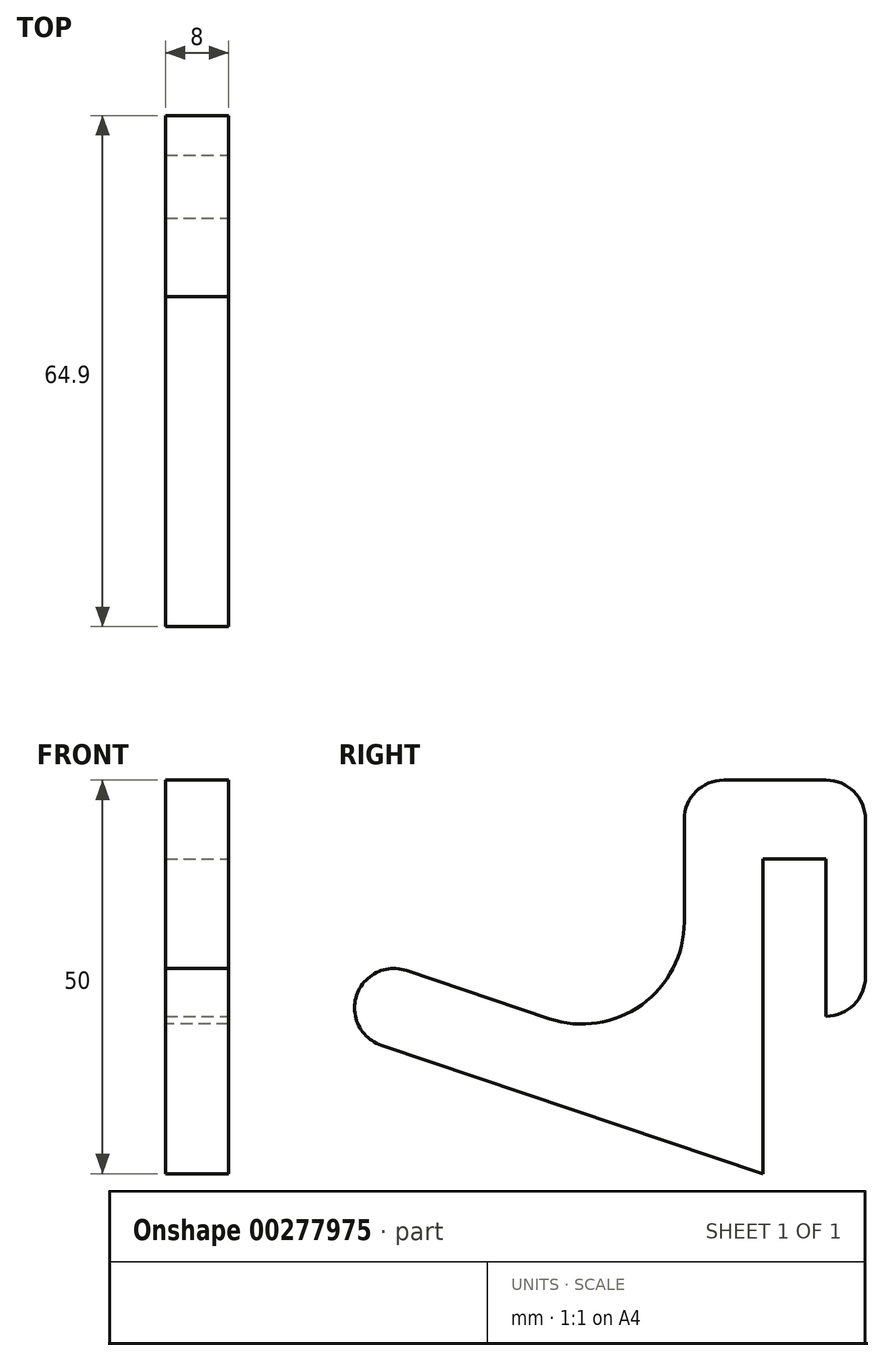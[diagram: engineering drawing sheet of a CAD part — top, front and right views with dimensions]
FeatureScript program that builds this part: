
annotation { "Feature Type Name" : "Feature", "Feature Type Description" : "" }
export const myFeature = defineFeature(function(context is Context, id is Id, definition is map)
    precondition{}
    {
        {
            var Q0;
            Q0=qCreatedBy(makeId("Right.planeOp"),FACE);
            var sketch = newSketch(context, id + "F0", { "sketchPlane" : qUnion([Q0])});
            skLineSegment(sketch, "E0", {"start": v(-11.66, 240.6) * mm, "end": v(-11.66, 204.52) * mm});
            skLineSegment(sketch, "E1", {"start": v(-1.66, 190.6) * mm, "end": v(-54.9, 208.51) * mm});
            skLineSegment(sketch, "E2.0", {"start": v(-11.66, 204.52) * mm, "end": v(-51.7, 217.99) * mm});
            skLineSegment(sketch, "E3", {"start": v(-51.7, 217.99) * mm, "end": v(-54.9, 208.51) * mm});
            skLineSegment(sketch, "E4", {"start": v(-1.66, 190.6) * mm, "end": v(-1.66, 230.6) * mm});
            skLineSegment(sketch, "E5", {"start": v(-1.66, 230.6) * mm, "end": v(6.34, 230.6) * mm});
            skLineSegment(sketch, "E6", {"start": v(6.34, 230.6) * mm, "end": v(6.34, 210.6) * mm});
            skLineSegment(sketch, "E7", {"start": v(6.34, 210.6) * mm, "end": v(11.34, 210.6) * mm});
            skLineSegment(sketch, "E8", {"start": v(11.34, 210.6) * mm, "end": v(11.34, 240.6) * mm});
            skLineSegment(sketch, "E9", {"start": v(11.34, 240.6) * mm, "end": v(-11.66, 240.6) * mm});
            skSolve(sketch);
        }
        {
            var Q0;
            Q0=qSketchRegion(id+"F0",true);
            extrude(context, id + "F1", {"entities" : qUnion([Q0]), "oppositeDirection" : true, "depth" : 8 * mm});
        }
        {
            var Q0;
            Q0=makeQuery(id+"F1.opExtrude","SWEPT_EDGE",EDGE,{"disambiguationData":[OSD([sQuery(id+"F0.wireOp",EDGE,"E2.0"),sQuery(id+"F0.wireOp",EDGE,"E3")])]});
            var Q1;
            Q1=makeQuery(id+"F1.opExtrude","SWEPT_EDGE",EDGE,{"disambiguationData":[OSD([sQuery(id+"F0.wireOp",EDGE,"E1"),sQuery(id+"F0.wireOp",EDGE,"E3")])]});
            fillet(context, id + "F2", {"entities" : qUnion([Q0, Q1]), "radius" : 5 * mm, "tangentPropagation" : true, "allowEdgeOverflow" : false});
        }
        {
            var Q0;
            Q0=makeQuery(id+"F1.opExtrude","SWEPT_EDGE",EDGE,{"disambiguationData":[OSD([sQuery(id+"F0.wireOp",EDGE,"E0"),sQuery(id+"F0.wireOp",EDGE,"E2.0")])]});
            fillet(context, id + "F3", {"entities" : qUnion([Q0]), "radius" : 13 * mm, "tangentPropagation" : true, "allowEdgeOverflow" : false});
        }
        {
            var Q0;
            Q0=makeQuery(id+"F1.opExtrude","SWEPT_EDGE",EDGE,{"disambiguationData":[OSD([sQuery(id+"F0.wireOp",EDGE,"E0"),sQuery(id+"F0.wireOp",EDGE,"E9")])]});
            var Q1;
            Q1=makeQuery(id+"F1.opExtrude","SWEPT_EDGE",EDGE,{"disambiguationData":[OSD([sQuery(id+"F0.wireOp",EDGE,"E8"),sQuery(id+"F0.wireOp",EDGE,"E9")])]});
            var Q2;
            Q2=makeQuery(id+"F1.opExtrude","SWEPT_EDGE",EDGE,{"disambiguationData":[OSD([sQuery(id+"F0.wireOp",EDGE,"E7"),sQuery(id+"F0.wireOp",EDGE,"E8")])]});
            fillet(context, id + "F4", {"entities" : qUnion([Q0, Q1, Q2]), "radius" : 5 * mm, "tangentPropagation" : true, "allowEdgeOverflow" : false});
        }
    });
